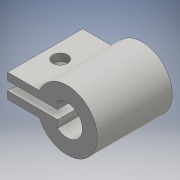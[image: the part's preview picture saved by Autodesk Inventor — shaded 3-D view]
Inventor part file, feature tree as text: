
AUTODESK INVENTOR PART (.ipt)
format: ipt  version: 2016 (Build 200138000, 138)  size: 124,928 bytes
history: native  units: mm
features: extrude x2, sketch x1
ambient origin geometry x8: Origin, YZ Plane, XZ Plane, XY Plane, X Axis, Y Axis, Z Axis, Center Point
bodies: Body1 (feature_tree)
feature tree (3):
  extrude  "Extrusion3"  Depth=15.0mm
  extrude  "Extrusion5"  Depth=1.5mm
  sketch  "Sketch3"  dims[d146=6.08mm d147=3.0mm d151=1.5mm d152=10.0mm d158=10.0mm d159=1.738175mm d160=3.238175mm d161=6.34901mm d162=6.34901mm d163=15.0mm d164=0.0mm d165=3.0mm d169=3.0mm d172=20.0mm d173=0.0mm]
